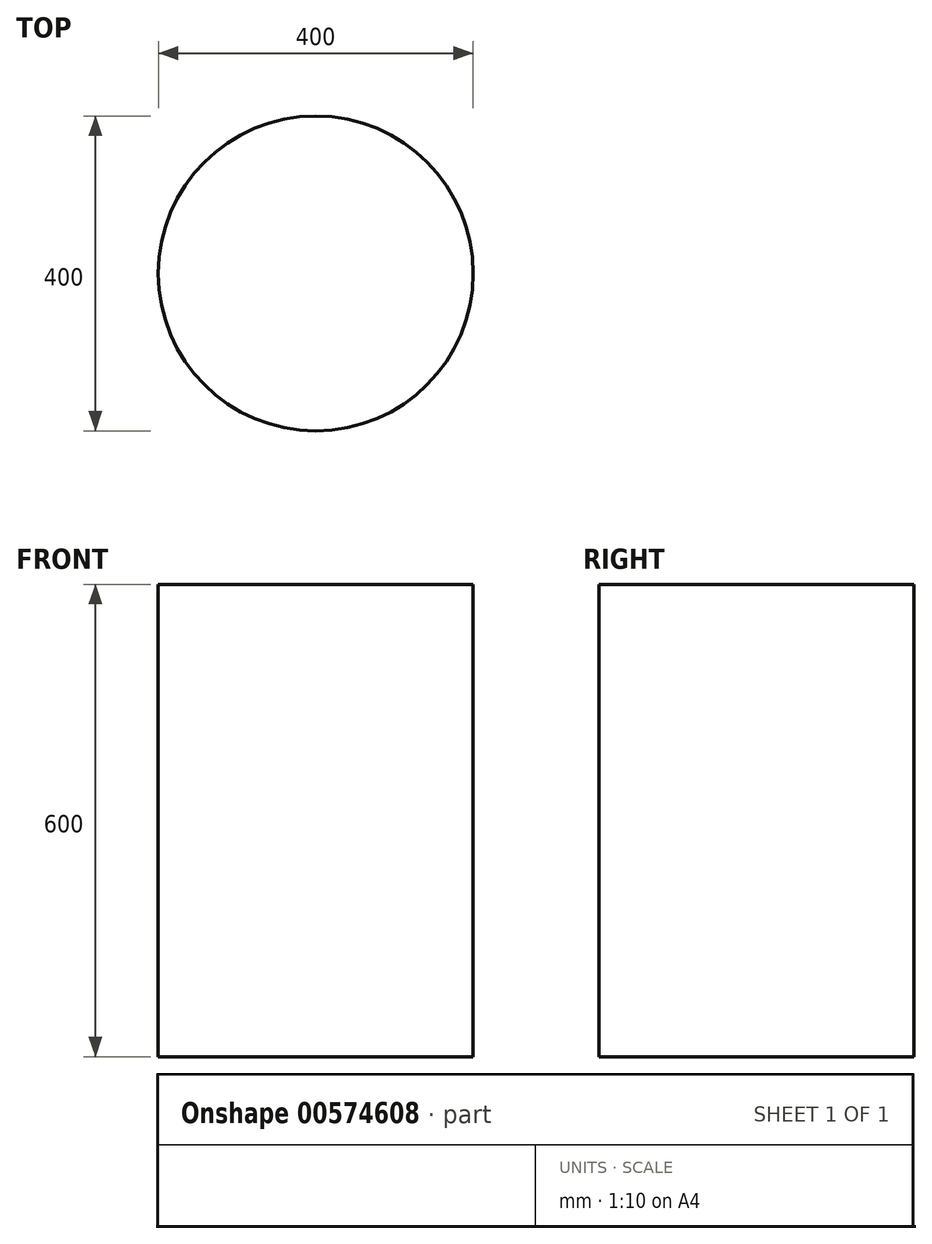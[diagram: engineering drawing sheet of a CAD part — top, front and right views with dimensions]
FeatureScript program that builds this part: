
annotation { "Feature Type Name" : "Feature", "Feature Type Description" : "" }
export const myFeature = defineFeature(function(context is Context, id is Id, definition is map)
    precondition{}
    {
        {
            var Q0;
            Q0=qCreatedBy(makeId("Front.planeOp"),FACE);
            var sketch = newSketch(context, id + "F0", { "sketchPlane" : qUnion([Q0])});
            skLineSegment(sketch, "E0", {"start": v(-200.4, 599.62) * mm, "end": v(-200.4, -0.38) * mm});
            skLineSegment(sketch, "E1", {"start": v(-200.4, -0.38) * mm, "end": v(199.6, -0.38) * mm});
            skLineSegment(sketch, "E2.0", {"start": v(199.6, 599.62) * mm, "end": v(199.6, -0.38) * mm});
            skLineSegment(sketch, "E3", {"start": v(-200.4, -0.38) * mm, "end": v(-200.4, 50.4) * mm});
            skLineSegment(sketch, "E4.0", {"start": v(-0.4, -251.76) * mm, "end": v(-0.4, -0.38) * mm});
            skLineSegment(sketch, "E5", {"start": v(-200.4, -0.38) * mm, "end": v(-0.4, -0.38) * mm});
            skLineSegment(sketch, "E6", {"start": v(-200.4, -0.38) * mm, "end": v(-100.4, -0.38) * mm});
            skSolve(sketch);
        }
        {
            var Q0;
            Q0=sQuery(id+"F0.wireOp",EDGE,"E0");
            var Q1;
            Q1=sQuery(id+"F0.wireOp",EDGE,"E4.0");
            revolve(context, id + "F1", {"bodyType" : ToolBodyType.SURFACE, "surfaceEntities" : qUnion([Q0]), "axis" : qUnion([Q1]), "revolveType" : RevolveType.FULL});
        }
        {
            var Q0;
            Q0=sQuery(id+"F0.wireOp",EDGE,"E5");
            var Q1;
            Q1=sQuery(id+"F0.wireOp",EDGE,"E4.0");
            revolve(context, id + "F2", {"bodyType" : ToolBodyType.SURFACE, "surfaceEntities" : qUnion([Q0]), "axis" : qUnion([Q1]), "revolveType" : RevolveType.FULL});
        }
    });
